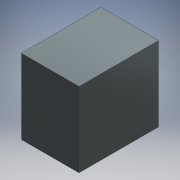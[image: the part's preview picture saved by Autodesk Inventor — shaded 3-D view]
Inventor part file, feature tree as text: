
AUTODESK INVENTOR PART (.ipt)
format: ipt  version: 2016 (Build 200138000, 138)  size: 168,960 bytes
history: native  units: mm
features: extrude x6, sketch x6
ambient origin geometry x8: Origin, YZ Plane, XZ Plane, XY Plane, X Axis, Y Axis, Z Axis, Center Point
bodies: Body1 (feature_tree)
feature tree (12):
  extrude  "Extrusion2"  Depth=548.0mm
  extrude  "Extrusion3"  Depth=583.0mm TaperAngle=0.0deg
  extrude  "Extrusion4"  Depth=345.0mm
  extrude  "Extrusion5"  Depth=88.0mm
  extrude  "Extrusion6"  Depth=75.0mm
  extrude  "Extrusion7"  Depth=583.0mm TaperAngle=0.0deg
  sketch  "Sketch1"  dims[d0=422.0mm d1=548.0mm]
  sketch  "Sketch2"  dims[d4=23.0mm d5=583.0mm d6=0.0mm]
  sketch  "Sketch3"  dims[d7=210.0mm d8=345.0mm]
  sketch  "Sketch4"  dims[d9=88.0mm d11=88.0mm]
  sketch  "Sketch5"  dims[d12=583.0mm d13=0.0mm d14=75.0mm]
  sketch  "Sketch6"  dims[d15=104.0mm d16=583.0mm d17=0.0mm d18=54.0mm d19=583.0mm d20=0.0mm d21=16.0mm d22=16.0mm d23=170.0mm d24=200.0mm d25=45.0mm d26=45.0mm d27=170.0mm d28=200.0mm d29=16.0mm d30=16.0mm d31=45.0mm d32=45.0mm d33=16.0mm d34=0.0mm d35=123.0mm d36=0.0mm]
